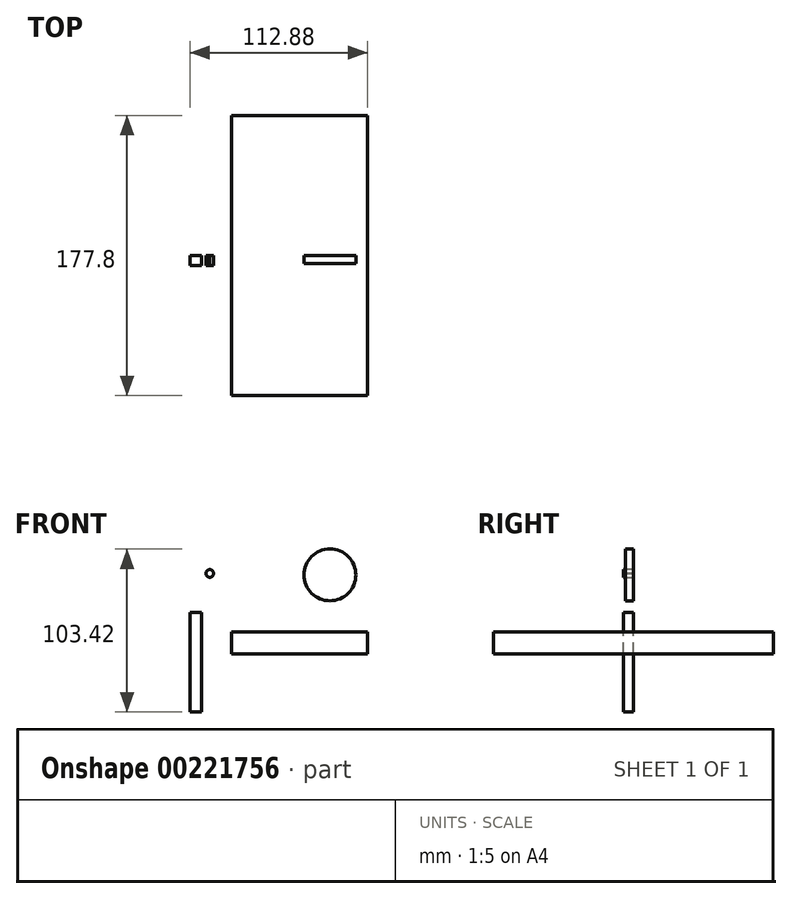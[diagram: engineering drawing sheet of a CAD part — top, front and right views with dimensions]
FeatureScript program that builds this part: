
annotation { "Feature Type Name" : "Feature", "Feature Type Description" : "" }
export const myFeature = defineFeature(function(context is Context, id is Id, definition is map)
    precondition{}
    {
        {
            var Q0;
            Q0=qCreatedBy(makeId("Front.planeOp"),FACE);
            var sketch = newSketch(context, id + "F0", { "sketchPlane" : qUnion([Q0])});
            skLineSegment(sketch, "E0.bottom", {"start": v(-41.09, 7.63) * mm, "end": v(45.42, 7.63) * mm});
            skLineSegment(sketch, "E0.top", {"start": v(-41.09, -6.5) * mm, "end": v(45.42, -6.5) * mm});
            skLineSegment(sketch, "E0.left", {"start": v(-41.09, 7.63) * mm, "end": v(-41.09, -6.5) * mm});
            skLineSegment(sketch, "E0.right", {"start": v(45.42, 7.63) * mm, "end": v(45.42, -6.5) * mm});
            skSolve(sketch);
        }
        {
            var Q0;
            Q0 = qSketchRegion(id + "F0", true);
            extrude(context, id + "F1", {"entities" : qUnion([Q0]), "depth" : 88.9 * mm});
        }
        {
            var Q0;
            Q0=makeQuery(id+"F1.opExtrude","SWEPT_BODY",BODY,{"disambiguationData":[OSD([sQuery(id+"F0.wireOp",EDGE,"E0.bottom"),sQuery(id+"F0.wireOp",EDGE,"E0.top"),sQuery(id+"F0.wireOp",EDGE,"E0.left"),sQuery(id+"F0.wireOp",EDGE,"E0.right")])]});
            var Q1;
            Q1=qCreatedBy(makeId("Front.planeOp"),FACE);
            mirror(context, id + "F2", {"operationType" : NewBodyOperationType.ADD, "entities" : qUnion([Q0]), "mirrorPlane" : qUnion([Q1])});
        }
        {
            var Q0;
            Q0=qCreatedBy(makeId("Front.planeOp"),FACE);
            var sketch = newSketch(context, id + "F3", { "sketchPlane" : qUnion([Q0])});
            skLineSegment(sketch, "E1", {"start": v(-67.46, -43.16) * mm, "end": v(-67.46, 19.98) * mm});
            skLineSegment(sketch, "E2", {"start": v(-67.46, -43.16) * mm, "end": v(-59.95, -43.16) * mm});
            skLineSegment(sketch, "E3", {"start": v(-59.95, -43.16) * mm, "end": v(-59.95, 19.98) * mm});
            skLineSegment(sketch, "E4", {"start": v(-67.46, 19.98) * mm, "end": v(-59.95, 19.98) * mm});
            skSolve(sketch);
        }
        {
            var Q0;
            Q0 = qSketchRegion(id + "F3", true);
            extrude(context, id + "F4", {"entities" : qUnion([Q0]), "depth" : 6.35 * mm});
        }
        {
            var Q0;
            Q0=qCreatedBy(makeId("Front.planeOp"),FACE);
            var sketch = newSketch(context, id + "F5", { "sketchPlane" : qUnion([Q0])});
            skCircle(sketch, "E5", {"center": v(21.49, 43.82) * mm, "radius": 16.44 * mm});
            skSolve(sketch);
        }
        {
            var Q0;
            Q0 = qSketchRegion(id + "F5", true);
            extrude(context, id + "F6", {"entities" : qUnion([Q0]), "depth" : 5.08 * mm});
        }
        {
            var Q0;
            Q0=qCreatedBy(makeId("Front.planeOp"),FACE);
            var sketch = newSketch(context, id + "F7", { "sketchPlane" : qUnion([Q0])});
            skLineSegment(sketch, "E6.bottom", {"start": v(-52.4, 42.31) * mm, "end": v(-57.3, 42.31) * mm});
            skLineSegment(sketch, "E6.top", {"start": v(-52.4, 47.21) * mm, "end": v(-57.3, 47.21) * mm});
            skLineSegment(sketch, "E6.left", {"start": v(-52.4, 42.31) * mm, "end": v(-52.4, 47.21) * mm});
            skLineSegment(sketch, "E6.right", {"start": v(-57.3, 42.31) * mm, "end": v(-57.3, 47.21) * mm});
            skPoint(sketch, "E6.middle", {"position": v(-54.85, 44.76) * mm});
            skSolve(sketch);
        }
        {
            var Q0;
            Q0 = qSketchRegion(id + "F7", true);
            extrude(context, id + "F8", {"entities" : qUnion([Q0]), "depth" : 6.35 * mm});
        }
        {
            var Q0;
            Q0=makeQuery(id+"F8.opExtrude","SWEPT_EDGE",EDGE,{"disambiguationData":[OSD([sQuery(id+"F7.wireOp",EDGE,"E6.top"),sQuery(id+"F7.wireOp",EDGE,"E6.right")])]});
            var Q1;
            Q1=makeQuery(id+"F8.opExtrude","SWEPT_EDGE",EDGE,{"disambiguationData":[OSD([sQuery(id+"F7.wireOp",EDGE,"E6.top"),sQuery(id+"F7.wireOp",EDGE,"E6.left")])]});
            var Q2;
            Q2=makeQuery(id+"F8.opExtrude","SWEPT_EDGE",EDGE,{"disambiguationData":[OSD([sQuery(id+"F7.wireOp",EDGE,"E6.bottom"),sQuery(id+"F7.wireOp",EDGE,"E6.right")])]});
            var Q3;
            Q3=makeQuery(id+"F8.opExtrude","SWEPT_EDGE",EDGE,{"disambiguationData":[OSD([sQuery(id+"F7.wireOp",EDGE,"E6.bottom"),sQuery(id+"F7.wireOp",EDGE,"E6.left")])]});
            fillet(context, id + "F9", {"entities" : qUnion([Q0, Q1, Q2, Q3]), "radius" : 2.54 * mm, "tangentPropagation" : true, "allowEdgeOverflow" : false});
        }
    });
